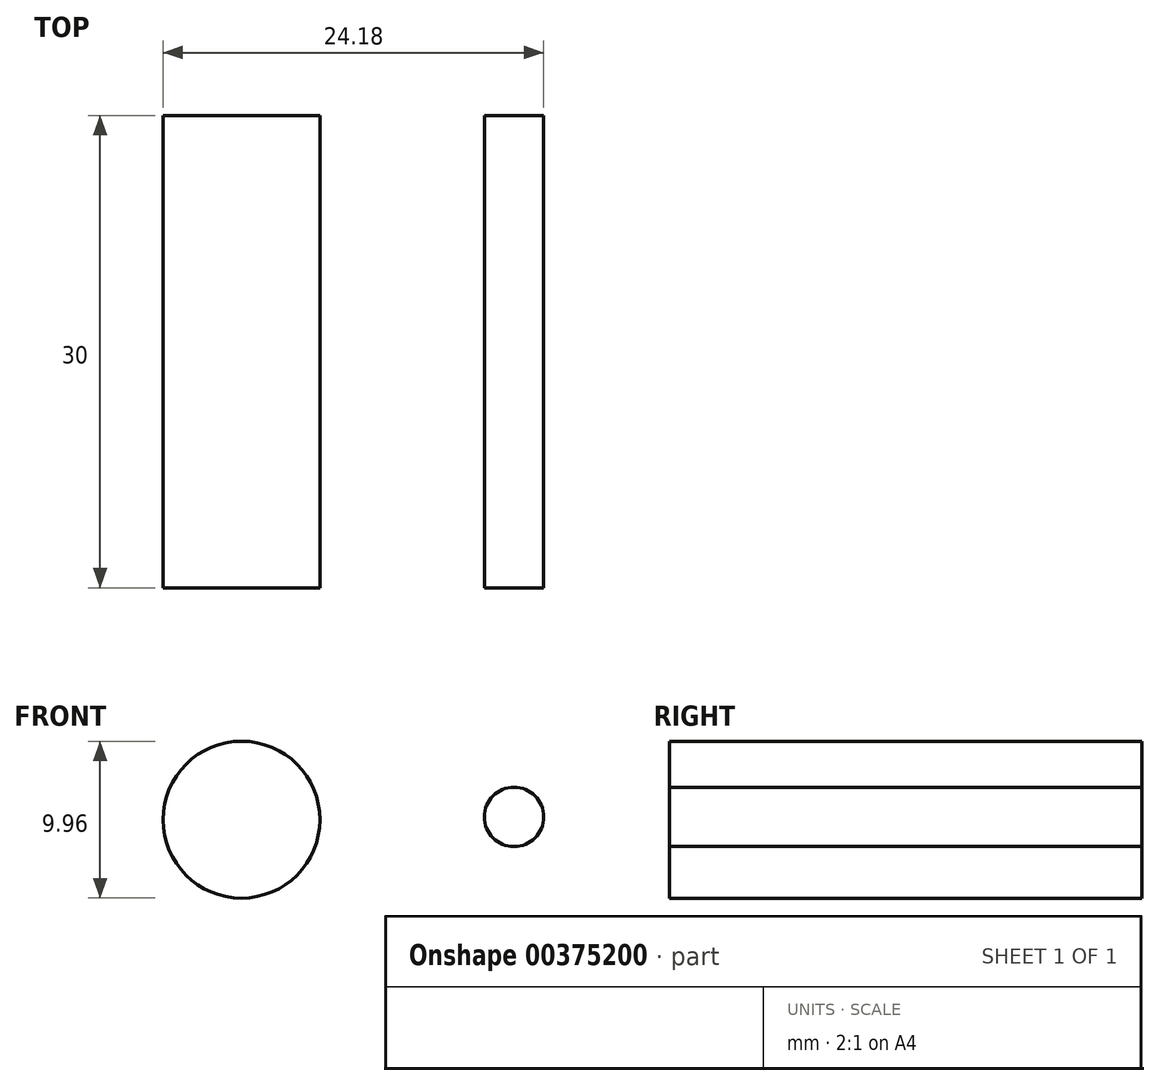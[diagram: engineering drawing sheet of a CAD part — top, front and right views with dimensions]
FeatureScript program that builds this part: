
annotation { "Feature Type Name" : "Feature", "Feature Type Description" : "" }
export const myFeature = defineFeature(function(context is Context, id is Id, definition is map)
    precondition{}
    {
        {
            var Q0;
            Q0=qCreatedBy(makeId("Front.planeOp"),FACE);
            var sketch = newSketch(context, id + "F0", { "sketchPlane" : qUnion([Q0])});
            skArc(sketch, "E0", {"start": v(-18.8, 56.06) * mm, "mid": v(1.23, 6.89) * mm, "end": v(21.28, 56.06) * mm});
            skSolve(sketch);
        }
        {
            var Q0;
            Q0=qCreatedBy(makeId("Front.planeOp"),FACE);
            var sketch = newSketch(context, id + "F1", { "sketchPlane" : qUnion([Q0])});
            skArc(sketch, "E1", {"start": v(21.28, 56.06) * mm, "mid": v(1.23, 76.3) * mm, "end": v(-18.8, 56.06) * mm});
            skSolve(sketch);
        }
        {
            var Q0;
            Q0=sQuery(id+"F0.wireOp",EDGE,"E0");
            extrude(context, id + "F2", {"bodyType" : ToolBodyType.SURFACE, "surfaceEntities" : qUnion([Q0]), "depth" : 25 * mm});
        }
        {
            var Q0;
            Q0=sQuery(id+"F1.wireOp",EDGE,"E1");
            extrude(context, id + "F3", {"bodyType" : ToolBodyType.SURFACE, "surfaceEntities" : qUnion([Q0]), "depth" : 25 * mm});
        }
        {
            var Q0;
            Q0=qCreatedBy(makeId("Front.planeOp"),FACE);
            var sketch = newSketch(context, id + "F4", { "sketchPlane" : qUnion([Q0])});
            skCircle(sketch, "E2", {"center": v(-8.66, 65.4) * mm, "radius": 4.98 * mm});
            skSolve(sketch);
        }
        {
            var Q0;
            Q0 = qSketchRegion(id + "F4", true);
            extrude(context, id + "F5", {"entities" : qUnion([Q0]), "depth" : 30 * mm});
        }
        {
            var Q0;
            Q0=qCreatedBy(makeId("Front.planeOp"),FACE);
            var sketch = newSketch(context, id + "F6", { "sketchPlane" : qUnion([Q0])});
            skCircle(sketch, "E3", {"center": v(8.66, 65.57) * mm, "radius": 1.88 * mm});
            skSolve(sketch);
        }
        {
            var Q0;
            Q0 = qSketchRegion(id + "F6", true);
            extrude(context, id + "F7", {"entities" : qUnion([Q0]), "depth" : 30 * mm});
        }
    });
